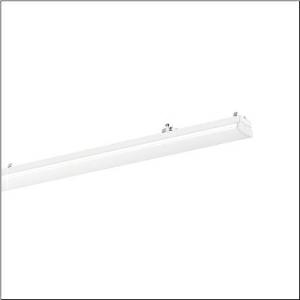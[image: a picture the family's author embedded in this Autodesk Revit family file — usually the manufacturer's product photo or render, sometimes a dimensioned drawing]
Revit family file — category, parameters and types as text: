
# Revit family: licross_r__11_recessed_opal_mo_51tl1dmn495g_9ece
name_source: partatom
category: Lighting Fixtures
units: mm (PartAtom-declared; Revit-internal decimal feet)

## family parameters
Cut with Voids When Loaded = No
Host = Face
Light Source = No
Part Type = Normal
Room Calculation Point = No
Round Connector Dimension = Use Diameter
Shared = No

## types (1)
- --- (1 x LED, 9750 lm, 55.2 W, 4000K)
    Apparent Load = 55 VA
    CIE Flux Codes = 44 73 91 87 100
    Color Rendering = 80
    Color Temperature = 4000K
    Default Elevation = 1800 mm
    Description = Licross® 11 recessed opal MO, luminaire insert, of sheet steel, coil coated, white, length: 1.500mm, width: 76mm, height: 87mm, LED rated luminous flux: 9.750lm, light colour: 840, control gear: ON/OFF Multilumen, with plug, 3-pole, with phase selection, mains connection: 220..240V, AC, 50/60Hz, rated input power: 55W, halogen-free wiring, primary optical cover: cover, of PMMA, light emission: direct with ceiling illumination distribution, primary light characteristic: symmetric, protection rating (complete): IP40, insulation class (complete): insulation class I (protective earthing), certification: CE, ENEC, VDE, UKCA, protection symbol: D if used in an environment without relevant dust loads with corresponding accessories, impact resistance: IK06, permissible ambient temperature for indoor applications: -35..+40°C, corresponds to IFS (International Featured Standards) requirements for safety and quality in the food industry, reducing of maximum allowable ambient temperature of 5°C with ceiling mounting, packaging unit: 1 piece
    Height = 83 mm
    Lamp = 1 x LED
    Lamp Light Flux = 9750 lm
    Lamp Power = 55.2 W
    Lamp count = 1
    Length = 1500 mm
    Luminous efficacy = 177 lm/W
    Manufacturer = Siteco
    ModVariant = No
    Model = 51TL1DMN495G
    Mounting Place = Ceiling
    Mounting Type = Pendant
    Number of Poles = 1
    OnlyDefault = Yes
    Power Factor = 1
    Product Name = Licross® 11 recessed opal MO
    Product group = luminaire insert
    ProductGroupID = 902
    Protection Class = Protection class I
    Protection Degree = IP 40
    RLX_Detail_Level = 1
    RLX_Emergency_Light_Flux = 0 lm
    RLX_Emergency_Type = 0
    RLX_Emergency_Type_DB = No
    RlxData = <blob elided: 24965 chars, md5=5453889d>
    Socket = socket
    Standby Power = 0 W
    System Light Flux = 9750 lm
    System Power = 55 W
    Type Comments = factory setting: luminous flux: 100 % | (A | C | E) | 126 mA
    Type Image = l_1313666.jpg
    URL = http://relux.com
    VarID = @adj_075832
    Voltage = 0 V
    Weight = 0.00 kg
    Width = 76 mm

## geometry (parser evidence)
native form markers: Blend x4, Sweep x10
no freeform markers — native parametric forms only
